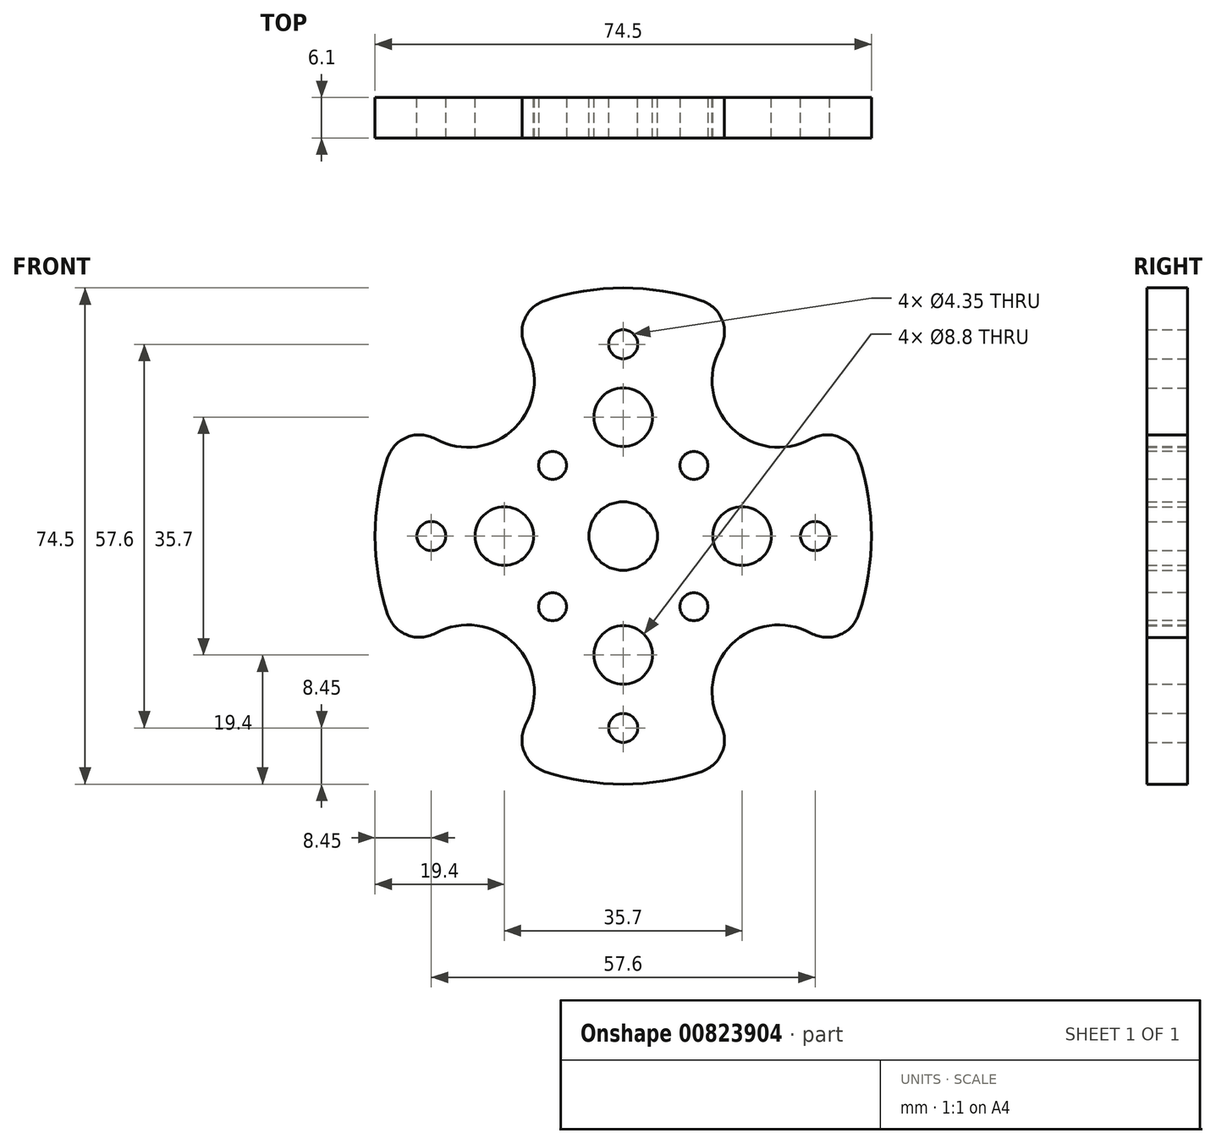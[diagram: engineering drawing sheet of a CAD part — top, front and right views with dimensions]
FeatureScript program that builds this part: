
annotation { "Feature Type Name" : "Feature", "Feature Type Description" : "" }
export const myFeature = defineFeature(function(context is Context, id is Id, definition is map)
    precondition{}
    {
        {
            var Q0;
            Q0=qCreatedBy(makeId("Front.planeOp"),FACE);
            var sketch = newSketch(context, id + "F0", { "sketchPlane" : qUnion([Q0])});
            skArc(sketch, "E0", {"start": v(-35.34, 11.79) * mm, "mid": v(-37.25, 0) * mm, "end": v(-35.34, -11.79) * mm});
            skLineSegment(sketch, "E1", {"start": v(0, 0) * mm, "end": v(-36, 36) * mm, "construction": true});
            skLineSegment(sketch, "E2", {"start": v(0, 0) * mm, "end": v(0, 60.76) * mm, "construction": true});
            skArc(sketch, "E3", {"start": v(-28.17, 14.58) * mm, "mid": v(-16.26, 16.26) * mm, "end": v(-14.58, 28.17) * mm});
            skArc(sketch, "E4.1.0", {"start": v(-14.58, -28.17) * mm, "mid": v(-16.26, -16.26) * mm, "end": v(-28.17, -14.58) * mm});
            skArc(sketch, "E4.2.0", {"start": v(28.17, -14.58) * mm, "mid": v(16.26, -16.26) * mm, "end": v(14.58, -28.17) * mm});
            skArc(sketch, "E4.3.0", {"start": v(14.58, 28.17) * mm, "mid": v(16.26, 16.26) * mm, "end": v(28.17, 14.58) * mm});
            skArc(sketch, "E5.trimOffspring", {"start": v(11.79, 35.34) * mm, "mid": v(0, 37.25) * mm, "end": v(-11.79, 35.34) * mm});
            skArc(sketch, "E6.trimOffspring", {"start": v(35.34, -11.79) * mm, "mid": v(37.25, 0) * mm, "end": v(35.34, 11.79) * mm});
            skArc(sketch, "E7.trimOffspring", {"start": v(-11.79, -35.34) * mm, "mid": v(0, -37.25) * mm, "end": v(11.79, -35.34) * mm});
            skPoint(sketch, "E8.visualSharp", {"position": v(18.72, 32.2) * mm});
            skArc(sketch, "E8.filletArc", {"start": v(14.58, 28.17) * mm, "mid": v(14.87, 32.4) * mm, "end": v(11.79, 35.34) * mm});
            skPoint(sketch, "E9.visualSharp", {"position": v(-18.72, 32.2) * mm});
            skArc(sketch, "E9.filletArc", {"start": v(-11.79, 35.34) * mm, "mid": v(-14.87, 32.4) * mm, "end": v(-14.58, 28.17) * mm});
            skPoint(sketch, "E10.visualSharp", {"position": v(32.2, -18.72) * mm});
            skArc(sketch, "E10.filletArc", {"start": v(28.17, -14.58) * mm, "mid": v(32.4, -14.87) * mm, "end": v(35.34, -11.79) * mm});
            skPoint(sketch, "E11.visualSharp", {"position": v(18.72, -32.2) * mm});
            skArc(sketch, "E11.filletArc", {"start": v(11.79, -35.34) * mm, "mid": v(14.87, -32.4) * mm, "end": v(14.58, -28.17) * mm});
            skPoint(sketch, "E12.visualSharp", {"position": v(-18.72, -32.2) * mm});
            skArc(sketch, "E12.filletArc", {"start": v(-14.58, -28.17) * mm, "mid": v(-14.87, -32.4) * mm, "end": v(-11.79, -35.34) * mm});
            skPoint(sketch, "E13.visualSharp", {"position": v(-32.2, -18.72) * mm});
            skArc(sketch, "E13.filletArc", {"start": v(-35.34, -11.79) * mm, "mid": v(-32.4, -14.87) * mm, "end": v(-28.17, -14.58) * mm});
            skPoint(sketch, "E14.visualSharp", {"position": v(-32.2, 18.72) * mm});
            skArc(sketch, "E14.filletArc", {"start": v(-28.17, 14.58) * mm, "mid": v(-32.4, 14.87) * mm, "end": v(-35.34, 11.79) * mm});
            skCircle(sketch, "E15", {"center": v(0, 0) * mm, "radius": 5.15 * mm});
            skCircle(sketch, "E16", {"center": v(0, 28.8) * mm, "radius": 2.17 * mm});
            skPoint(sketch, "E17.centerSnap0", {"position": v(-16.26, 16.26) * mm});
            skCircle(sketch, "E18", {"center": v(0, 17.85) * mm, "radius": 4.4 * mm});
            skCircle(sketch, "E19.1.0", {"center": v(-17.85, 0) * mm, "radius": 4.4 * mm});
            skCircle(sketch, "E19.1.1", {"center": v(-28.8, 0) * mm, "radius": 2.17 * mm});
            skCircle(sketch, "E19.2.0", {"center": v(0, -17.85) * mm, "radius": 4.4 * mm});
            skCircle(sketch, "E19.2.1", {"center": v(0, -28.8) * mm, "radius": 2.17 * mm});
            skCircle(sketch, "E19.3.0", {"center": v(17.85, 0) * mm, "radius": 4.4 * mm});
            skCircle(sketch, "E19.3.1", {"center": v(28.8, 0) * mm, "radius": 2.17 * mm});
            skPoint(sketch, "E20.visualSharp", {"position": v(32.2, 18.72) * mm});
            skArc(sketch, "E20.filletArc", {"start": v(35.34, 11.79) * mm, "mid": v(32.4, 14.87) * mm, "end": v(28.17, 14.58) * mm});
            skSolve(sketch);
        }
        {
            var Q0;
            Q0 = qSketchRegion(id + "F0", true);
            extrude(context, id + "F1", {"entities" : qUnion([Q0]), "depth" : 6.1 * mm, "offsetDistance" : 25 * mm});
        }
        {
            var Q0;
            Q0=makeQuery(id+"F1.opExtrude","CAP_FACE",FACE,{"disambiguationData":[OSD([sQuery(id+"F0.wireOp",EDGE,"E0"),sQuery(id+"F0.wireOp",EDGE,"E3"),sQuery(id+"F0.wireOp",EDGE,"E4.1.0"),sQuery(id+"F0.wireOp",EDGE,"E4.2.0"),sQuery(id+"F0.wireOp",EDGE,"E4.3.0"),sQuery(id+"F0.wireOp",EDGE,"E5.trimOffspring"),sQuery(id+"F0.wireOp",EDGE,"E6.trimOffspring"),sQuery(id+"F0.wireOp",EDGE,"E7.trimOffspring"),sQuery(id+"F0.wireOp",EDGE,"E8.filletArc"),sQuery(id+"F0.wireOp",EDGE,"E9.filletArc"),sQuery(id+"F0.wireOp",EDGE,"E10.filletArc"),sQuery(id+"F0.wireOp",EDGE,"E11.filletArc"),sQuery(id+"F0.wireOp",EDGE,"E12.filletArc"),sQuery(id+"F0.wireOp",EDGE,"E13.filletArc"),sQuery(id+"F0.wireOp",EDGE,"E14.filletArc"),sQuery(id+"F0.wireOp",EDGE,"E15"),sQuery(id+"F0.wireOp",EDGE,"E16"),sQuery(id+"F0.wireOp",EDGE,"E18"),sQuery(id+"F0.wireOp",EDGE,"E19.1.0"),sQuery(id+"F0.wireOp",EDGE,"E19.1.1"),sQuery(id+"F0.wireOp",EDGE,"E19.2.0"),sQuery(id+"F0.wireOp",EDGE,"E19.2.1"),sQuery(id+"F0.wireOp",EDGE,"E19.3.0"),sQuery(id+"F0.wireOp",EDGE,"E19.3.1")])],"isStart":false});
            var sketch = newSketch(context, id + "F2", { "sketchPlane" : qUnion([Q0])});
            skLineSegment(sketch, "E21", {"start": v(0, 0) * mm, "end": v(0, 25.38) * mm, "construction": true});
            skLineSegment(sketch, "E22", {"start": v(0, 0) * mm, "end": v(-27.98, 0) * mm, "construction": true});
            skCircle(sketch, "E23", {"center": v(0, 0) * mm, "radius": 15 * mm, "construction": true});
            skLineSegment(sketch, "E24", {"start": v(0, 0) * mm, "end": v(-26.44, 26.44) * mm, "construction": true});
            skCircle(sketch, "E25", {"center": v(-10.6, 10.6) * mm, "radius": 2.1 * mm});
            skCircle(sketch, "E26.1.0", {"center": v(-10.6, -10.6) * mm, "radius": 2.1 * mm});
            skCircle(sketch, "E26.2.0", {"center": v(10.6, -10.6) * mm, "radius": 2.1 * mm});
            skCircle(sketch, "E26.3.0", {"center": v(10.6, 10.6) * mm, "radius": 2.1 * mm});
            skSolve(sketch);
        }
        {
            var Q0;
            Q0 = qSketchRegion(id + "F2", true);
            extrude(context, id + "F3", {"entities" : qUnion([Q0]), "operationType" : NewBodyOperationType.REMOVE, "endBound" : BoundingType.THROUGH_ALL, "oppositeDirection" : true, "depth" : 25 * mm, "offsetDistance" : 25 * mm});
        }
    });
